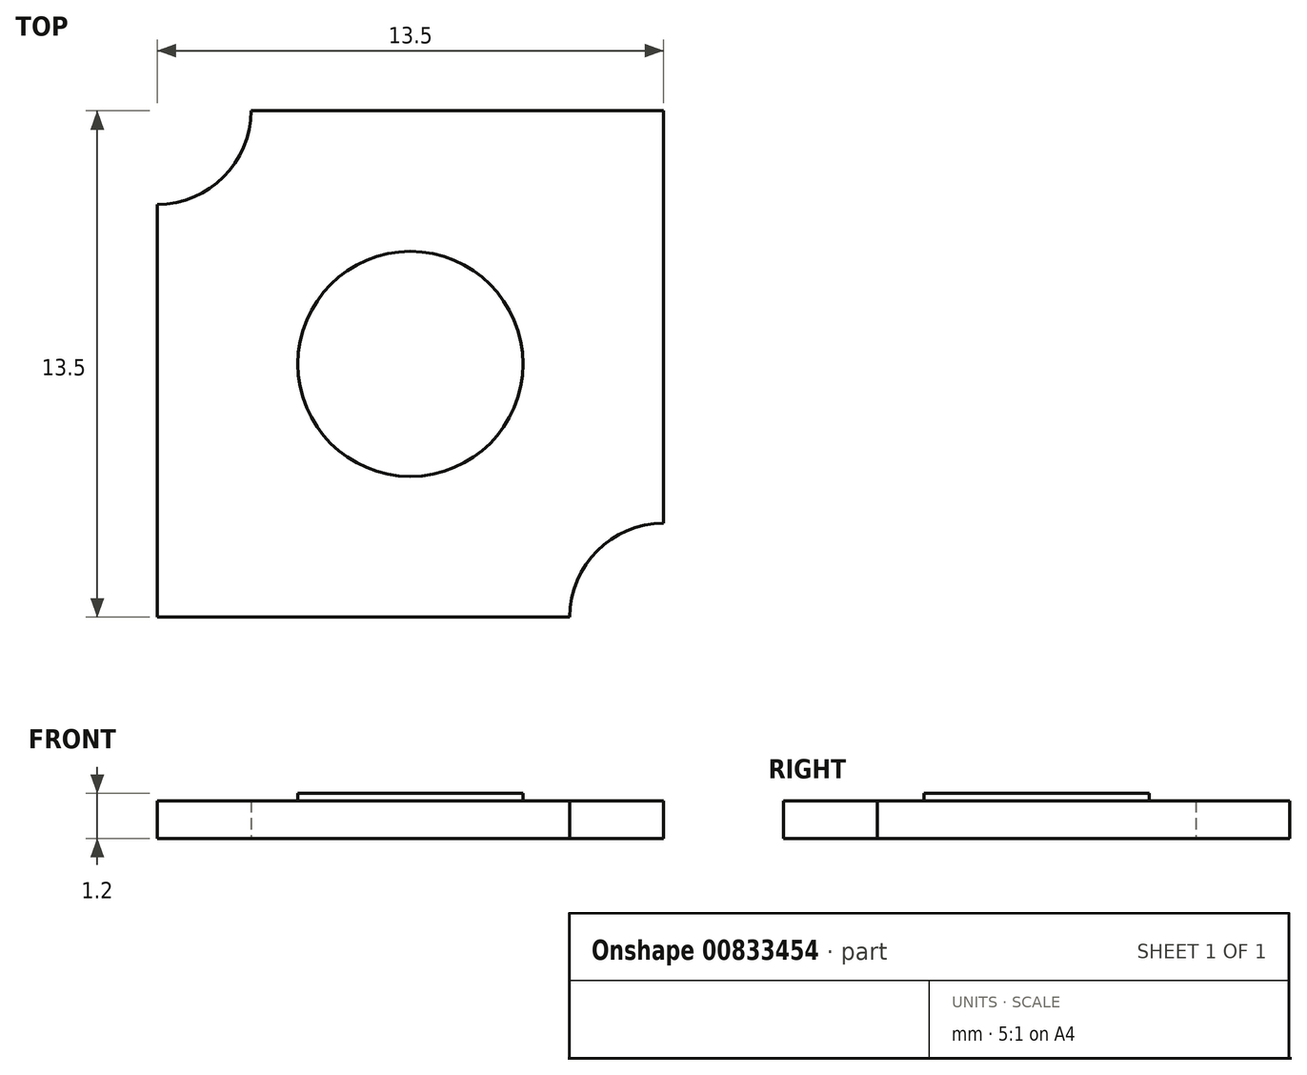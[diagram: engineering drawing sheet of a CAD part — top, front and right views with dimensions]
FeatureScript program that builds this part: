
annotation { "Feature Type Name" : "Feature", "Feature Type Description" : "" }
export const myFeature = defineFeature(function(context is Context, id is Id, definition is map)
    precondition{}
    {
        {
            var Q0;
            Q0=qCreatedBy(makeId("Top.planeOp"),FACE);
            var sketch = newSketch(context, id + "F0", { "sketchPlane" : qUnion([Q0])});
            skLineSegment(sketch, "E0.bottom", {"start": v(6.75, -6.75) * mm, "end": v(-6.75, -6.75) * mm});
            skLineSegment(sketch, "E0.top", {"start": v(6.75, 6.75) * mm, "end": v(-6.75, 6.75) * mm});
            skLineSegment(sketch, "E0.left", {"start": v(6.75, -6.75) * mm, "end": v(6.75, 6.75) * mm});
            skLineSegment(sketch, "E0.right", {"start": v(-6.75, -6.75) * mm, "end": v(-6.75, 6.75) * mm});
            skPoint(sketch, "E0.middle", {"position": v(0, 0) * mm});
            skCircle(sketch, "E1", {"center": v(0, 0) * mm, "radius": 3 * mm});
            skCircle(sketch, "E2", {"center": v(-6.75, 6.75) * mm, "radius": 2.5 * mm});
            skCircle(sketch, "E3", {"center": v(6.75, -6.75) * mm, "radius": 2.5 * mm});
            skSolve(sketch);
        }
        {
            var Q0;
            Q0=makeQuery(id+"F0.imprint","IMPRINT",FACE,{"disambiguationData":[TD([[makeQuery(id+"F0.imprint","IMPRINT",EDGE,{"derivedFrom":sQuery(id+"F0.wireOp",EDGE,"E1")}),-1.0]])]});
            var Q1;
            Q1=makeQuery(id+"F0.imprint","IMPRINT",FACE,{"disambiguationData":[TD([[makeQuery(id+"F0.imprint","IMPRINT",EDGE,{"derivedFrom":sQuery(id+"F0.wireOp",EDGE,"E1")}),1.0]])]});
            extrude(context, id + "F1", {"entities" : qUnion([Q0, Q1]), "depth" : 1 * mm, "offsetDistance" : 25 * mm});
        }
        {
            var Q0;
            Q0=makeQuery(id+"F0.imprint","IMPRINT",FACE,{"disambiguationData":[TD([[makeQuery(id+"F0.imprint","IMPRINT",EDGE,{"derivedFrom":sQuery(id+"F0.wireOp",EDGE,"E1")}),1.0]])]});
            extrude(context, id + "F2", {"entities" : qUnion([Q0]), "operationType" : NewBodyOperationType.ADD, "depth" : 1.2 * mm, "offsetDistance" : 25 * mm});
        }
    });
